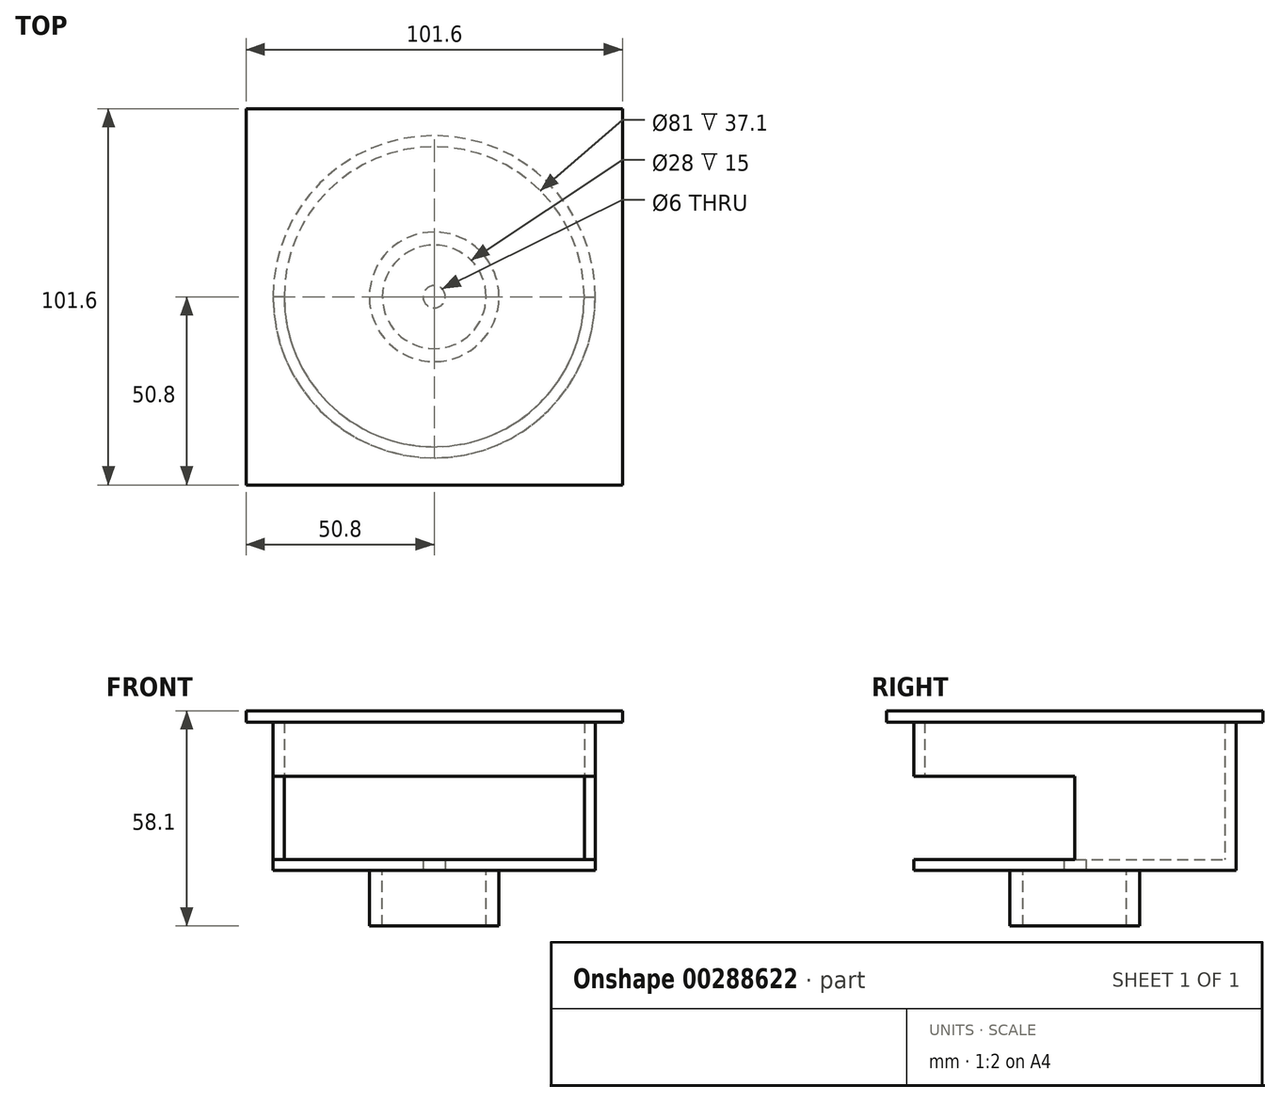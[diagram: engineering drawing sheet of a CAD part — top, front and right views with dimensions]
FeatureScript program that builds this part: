
annotation { "Feature Type Name" : "Feature", "Feature Type Description" : "" }
export const myFeature = defineFeature(function(context is Context, id is Id, definition is map)
    precondition{}
    {
        {
            var Q0;
            Q0=qCreatedBy(makeId("Top.planeOp"),FACE);
            var sketch = newSketch(context, id + "F0", { "sketchPlane" : qUnion([Q0])});
            skCircle(sketch, "E0", {"center": v(0, 0) * mm, "radius": 43.5 * mm});
            skArc(sketch, "E1", {"start": v(40.5, 0) * mm, "mid": v(0, 40.5) * mm, "end": v(-40.5, 0) * mm});
            skLineSegment(sketch, "E2", {"start": v(-40.5, 0) * mm, "end": v(-43.5, 0) * mm});
            skLineSegment(sketch, "E3", {"start": v(0, 40.5) * mm, "end": v(0, 43.5) * mm});
            skPoint(sketch, "E3.startSnap0", {"position": v(0, 40.5) * mm});
            skLineSegment(sketch, "E4", {"start": v(40.5, 0) * mm, "end": v(43.5, 0) * mm});
            skSolve(sketch);
        }
        {
            var Q0;
            {var subQ0=sQuery(id+"F0.wireOp",EDGE,"E2");Q0=makeQuery(id+"F0.imprint","IMPRINT",FACE,{"disambiguationData":[TD([[makeQuery(id+"F0.imprint","IMPRINT",EDGE,{"derivedFrom":subQ0}),-1.0]])]});}
            var Q1;
            {var subQ0=sQuery(id+"F0.wireOp",EDGE,"E3");Q1=makeQuery(id+"F0.imprint","IMPRINT",FACE,{"disambiguationData":[TD([[makeQuery(id+"F0.imprint","IMPRINT",EDGE,{"derivedFrom":subQ0}),-1.0]])]});}
            extrude(context, id + "F1", {"entities" : qUnion([Q0, Q1]), "depth" : 25.4 * mm});
        }
        {
            var Q0;
            {var subQ0=sQuery(id+"F0.wireOp",EDGE,"E2");Q0=makeQuery(id+"F0.imprint","IMPRINT",FACE,{"disambiguationData":[TD([[makeQuery(id+"F0.imprint","IMPRINT",EDGE,{"derivedFrom":subQ0}),1.0]])]});}
            extrude(context, id + "F2", {"entities" : qUnion([Q0]), "depth" : 3 * mm});
        }
        {
            var Q0;
            Q0=makeQuery(id+"F1.opExtrude","CAP_FACE",FACE,{"disambiguationData":[OSD([sQuery(id+"F0.wireOp",EDGE,"E0"),sQuery(id+"F0.wireOp",EDGE,"E1"),sQuery(id+"F0.wireOp",EDGE,"E2"),sQuery(id+"F0.wireOp",EDGE,"E4")])],"isStart":false});
            var sketch = newSketch(context, id + "F3", { "sketchPlane" : qUnion([Q0])});
            skCircle(sketch, "E5", {"center": v(0, 0) * mm, "radius": 43.5 * mm});
            skCircle(sketch, "E6", {"center": v(0, 0) * mm, "radius": 40.5 * mm});
            skSolve(sketch);
        }
        {
            var Q0;
            Q0=qSketchRegion(id+"F3",true);
            var Q1;
            Q1=makeQuery(id+"F3.imprint","IMPRINT",FACE,{"disambiguationData":[TD([[makeQuery(id+"F3.imprint","IMPRINT",EDGE,{"derivedFrom":sQuery(id+"F3.wireOp",EDGE,"zAPqjtf7-BBeI-U8aq-vM74-lsi97plc3mBI")}),1.0]])]});
            extrude(context, id + "F4", {"entities" : qUnion([Q0, Q1]), "operationType" : NewBodyOperationType.ADD, "depth" : 2 * mm});
        }
        {
            var Q0;
            Q0=makeQuery(id+"F4.opExtrude","CAP_FACE",FACE,{"disambiguationData":[OSD([sQuery(id+"F3.wireOp",EDGE,"E5")])],"isStart":false});
            var sketch = newSketch(context, id + "F5", { "sketchPlane" : qUnion([Q0])});
            skCircle(sketch, "E7", {"center": v(0, 0) * mm, "radius": 43.5 * mm});
            skSolve(sketch);
        }
        {
            var Q0;
            Q0=makeQuery(id+"F5.imprint","IMPRINT",FACE,{"disambiguationData":[TD([[makeQuery(id+"F5.imprint","IMPRINT",EDGE,{"derivedFrom":sQuery(id+"F5.wireOp",EDGE,"E7")}),1.0]])]});
            extrude(context, id + "F6", {"entities" : qUnion([Q0]), "operationType" : NewBodyOperationType.ADD, "depth" : 12.7 * mm});
        }
        {
            var Q0;
            Q0=makeQuery(id+"F6.opExtrude","CAP_FACE",FACE,{"disambiguationData":[OSD([sQuery(id+"F5.wireOp",EDGE,"E7")])],"isStart":false});
            var sketch = newSketch(context, id + "F7", { "sketchPlane" : qUnion([Q0])});
            skLineSegment(sketch, "E8.bottom", {"start": v(50.8, 50.8) * mm, "end": v(-50.8, 50.8) * mm});
            skLineSegment(sketch, "E8.top", {"start": v(50.8, -50.8) * mm, "end": v(-50.8, -50.8) * mm});
            skLineSegment(sketch, "E8.left", {"start": v(50.8, 50.8) * mm, "end": v(50.8, -50.8) * mm});
            skLineSegment(sketch, "E8.right", {"start": v(-50.8, 50.8) * mm, "end": v(-50.8, -50.8) * mm});
            skPoint(sketch, "E8.middle", {"position": v(0, 0) * mm});
            skSolve(sketch);
        }
        {
            var Q0;
            Q0=qSketchRegion(id+"F7",true);
            extrude(context, id + "F8", {"entities" : qUnion([Q0]), "operationType" : NewBodyOperationType.ADD, "depth" : 3 * mm});
        }
        {
            var Q0;
            {var subQ0=sQuery(id+"F0.wireOp",EDGE,"E2");Q0=makeQuery(id+"F0.imprint","IMPRINT",FACE,{"disambiguationData":[TD([[makeQuery(id+"F0.imprint","IMPRINT",EDGE,{"derivedFrom":subQ0}),1.0]])]});}
            var sketch = newSketch(context, id + "F9", { "sketchPlane" : qUnion([Q0])});
            skCircle(sketch, "E9", {"center": v(0, 0) * mm, "radius": 14 * mm});
            skCircle(sketch, "E10", {"center": v(0, 0) * mm, "radius": 17.5 * mm});
            skSolve(sketch);
        }
        {
            var Q0;
            Q0 = qSketchRegion(id + "F9", true);
            extrude(context, id + "F10", {"entities" : qUnion([Q0]), "operationType" : NewBodyOperationType.ADD, "oppositeDirection" : true, "depth" : 15 * mm});
        }
        {
            var Q0;
            Q0=sQuery(id+"F0.wireOp",VERTEX,"E1.center");
            var Q1;
            Q1=makeQuery(id+"F2.opExtrude","SWEPT_BODY",BODY,{"disambiguationData":[OSD([sQuery(id+"F0.wireOp",EDGE,"E0"),sQuery(id+"F0.wireOp",EDGE,"E1"),sQuery(id+"F0.wireOp",EDGE,"E2"),sQuery(id+"F0.wireOp",EDGE,"E4")])]});
            hole(context, id + "F11", {"style" : HoleStyle.SIMPLE, "endStyle" : HoleEndStyle.BLIND, "oppositeDirection" : true, "holeDiameter" : 6 * mm, "holeDepth" : 20 * mm, "isTappedThrough" : true, "tappedDepth" : 12 * mm, "tapClearance" : 3, "locations" : qUnion([Q0]), "scope" : qUnion([Q1])});
        }
        {
            var Q0;
            {var subQ0=sQuery(id+"F0.wireOp",EDGE,"E2");Q0=makeQuery(id+"F0.imprint","IMPRINT",FACE,{"disambiguationData":[TD([[makeQuery(id+"F0.imprint","IMPRINT",EDGE,{"derivedFrom":subQ0}),-1.0]])]});}
            var Q1;
            {var subQ0=sQuery(id+"F0.wireOp",EDGE,"E3");Q1=makeQuery(id+"F0.imprint","IMPRINT",FACE,{"disambiguationData":[TD([[makeQuery(id+"F0.imprint","IMPRINT",EDGE,{"derivedFrom":subQ0}),-1.0]])]});}
            extrude(context, id + "F12", {"entities" : qUnion([Q0, Q1]), "operationType" : NewBodyOperationType.ADD, "depth" : 3 * mm});
        }
    });
